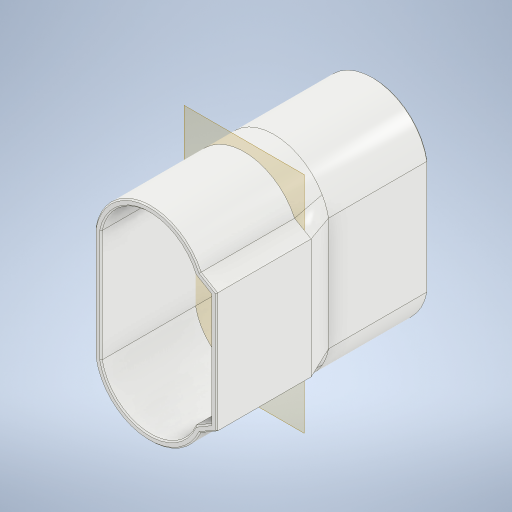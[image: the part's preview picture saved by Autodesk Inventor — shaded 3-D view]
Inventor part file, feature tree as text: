
AUTODESK INVENTOR PART (.ipt)
format: ipt  version: 2024.2 (Build 282272000, 272)  size: 1,177,600 bytes
history: native  units: in
note: dims shown in document units (in); Inventor stores cm internally (conversion verified against a paired STEP export)
features: sketch x3, extrude x3, other x2, plane x1, loft x1, shell x1, fillet x1, chamfer x1
ambient origin geometry x8: Origin, YZ Plane, XZ Plane, XY Plane, X Axis, Y Axis, Z Axis, Center Point
bodies: Solid1 (feature_tree)
feature tree (13):
  sketch  "Sketch1"  dims[d4=0.4724in d5=1.7898in]
  plane  "Work Plane1"
  extrude  "Extrusion1"  Depth=1.7898in
  extrude  "Extrusion2"  Depth=1.5748in TaperAngle=0.0deg
  loft  "Loft1"
  shell  "Shell2"  Thickness=0.0945in
  extrude  "Extrusion3"  Depth=0.1181in
  fillet  "Fillet1"  Radius=0.7874in
  chamfer  "Chamfer1"  Distance=0.0394in
  sketch  "Sketch2"  dims[d12=1.4961in d13=0.0in d14=1.5748in d15=0.0in]
  other  "Edges1"
  other  "Edges2"
  sketch  "Sketch3"  dims[d16=0.0in d17=90.0deg d18=0.0in d19=90.0deg d21=0.0945in d23=0.1181in d24=0.7874in d25=0.7874in d26=0.0in d27=0.0in d28=0.0394in d29=0.0197in d30=0.0787in d31=45.0deg]
